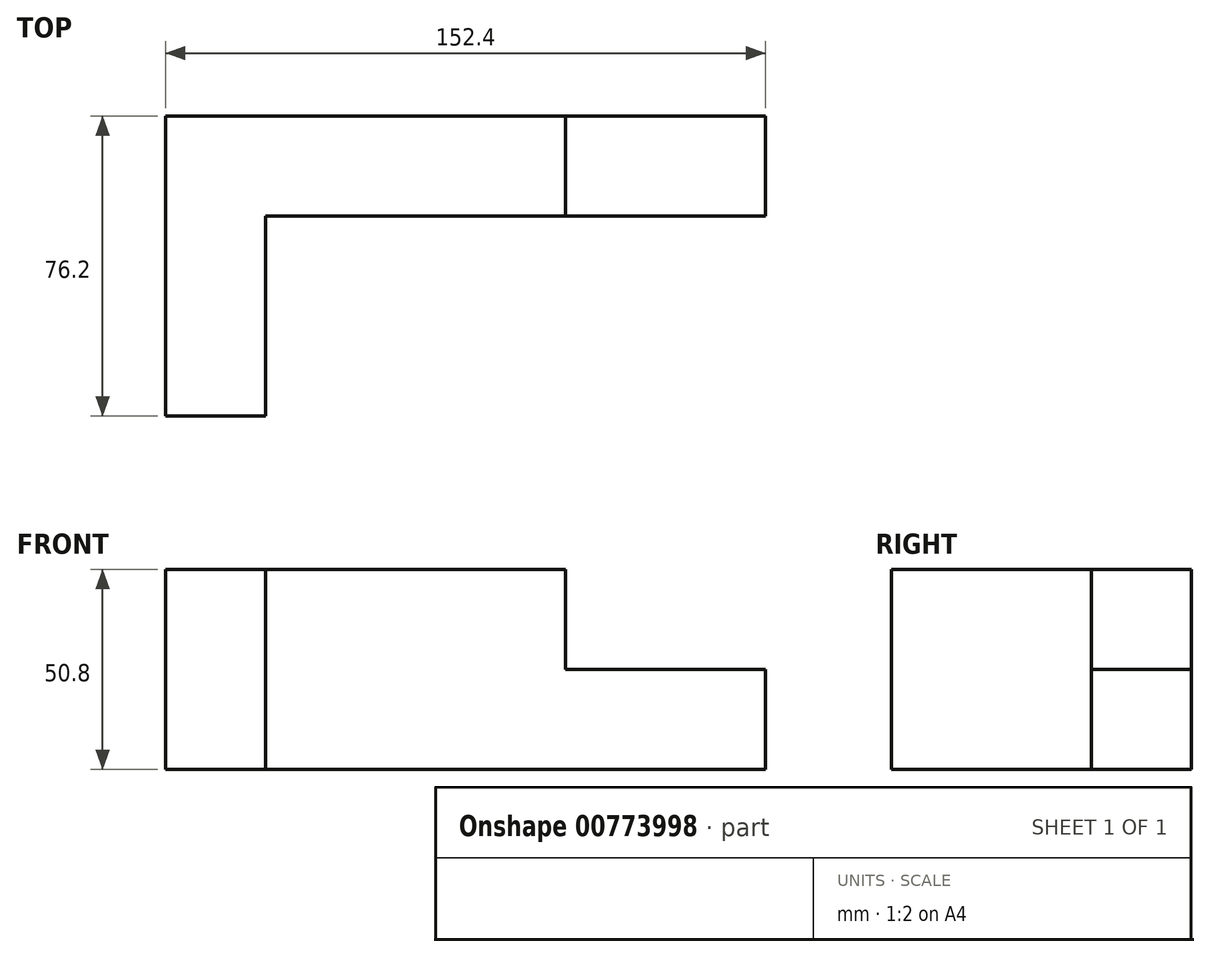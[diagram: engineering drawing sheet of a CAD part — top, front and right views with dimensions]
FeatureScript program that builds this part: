
annotation { "Feature Type Name" : "Feature", "Feature Type Description" : "" }
export const myFeature = defineFeature(function(context is Context, id is Id, definition is map)
    precondition{}
    {
        {
            var Q0;
            Q0=qCreatedBy(makeId("Front.planeOp"),FACE);
            var sketch = newSketch(context, id + "F0", { "sketchPlane" : qUnion([Q0])});
            skLineSegment(sketch, "E0", {"start": v(0, 0) * mm, "end": v(152.4, 0) * mm});
            skLineSegment(sketch, "E1", {"start": v(152.4, 0) * mm, "end": v(152.4, 50.8) * mm});
            skLineSegment(sketch, "E2", {"start": v(152.4, 50.8) * mm, "end": v(0, 50.8) * mm});
            skLineSegment(sketch, "E3", {"start": v(0, 50.8) * mm, "end": v(0, 0) * mm});
            skSolve(sketch);
        }
        {
            var Q0;
            Q0=makeQuery(id+"F0.imprint","IMPRINT",FACE,{"disambiguationData":[TD([[makeQuery(id+"F0.imprint","IMPRINT",EDGE,{"derivedFrom":sQuery(id+"F0.wireOp",EDGE,"E0")}),1.0]])]});
            extrude(context, id + "F1", {"entities" : qUnion([Q0]), "depth" : 76.2 * mm, "offsetDistance" : 25.4 * mm});
        }
        {
            var Q0;
            Q0=makeQuery(id+"F1.opExtrude","CAP_FACE",FACE,{"disambiguationData":[OSD([sQuery(id+"F0.wireOp",EDGE,"E0"),sQuery(id+"F0.wireOp",EDGE,"E1"),sQuery(id+"F0.wireOp",EDGE,"E2"),sQuery(id+"F0.wireOp",EDGE,"E3")])],"isStart":false});
            var sketch = newSketch(context, id + "F2", { "sketchPlane" : qUnion([Q0])});
            skLineSegment(sketch, "E4", {"start": v(152.4, 0) * mm, "end": v(152.4, 50.8) * mm});
            skLineSegment(sketch, "E5", {"start": v(152.4, 50.8) * mm, "end": v(25.4, 50.8) * mm});
            skLineSegment(sketch, "E6", {"start": v(25.4, 50.8) * mm, "end": v(25.4, 0) * mm});
            skLineSegment(sketch, "E7", {"start": v(25.4, 0) * mm, "end": v(152.4, 0) * mm});
            skSolve(sketch);
        }
        {
            var Q0;
            Q0=makeQuery(id+"F2.imprint","IMPRINT",FACE,{"disambiguationData":[TD([[makeQuery(id+"F2.imprint","IMPRINT",EDGE,{"derivedFrom":sQuery(id+"F2.wireOp",EDGE,"E4")}),1.0]])]});
            extrude(context, id + "F3", {"entities" : qUnion([Q0]), "operationType" : NewBodyOperationType.REMOVE, "oppositeDirection" : true, "depth" : 50.8 * mm, "offsetDistance" : 25.4 * mm});
        }
        {
            var Q0;
            Q0=makeQuery(id+"F3.boolean.opBoolean","COPY",FACE,{"derivedFrom":makeQuery(id+"F3.opExtrude","CAP_FACE",FACE,{"disambiguationData":[OSD([sQuery(id+"F2.wireOp",EDGE,"E4"),sQuery(id+"F2.wireOp",EDGE,"E5"),sQuery(id+"F2.wireOp",EDGE,"E6"),sQuery(id+"F2.wireOp",EDGE,"E7")])],"isStart":false})});
            var sketch = newSketch(context, id + "F4", { "sketchPlane" : qUnion([Q0])});
            skLineSegment(sketch, "E8", {"start": v(152.4, 50.8) * mm, "end": v(152.4, 25.4) * mm});
            skLineSegment(sketch, "E9", {"start": v(152.4, 25.4) * mm, "end": v(101.6, 25.4) * mm});
            skLineSegment(sketch, "E10", {"start": v(101.6, 25.4) * mm, "end": v(101.6, 50.8) * mm});
            skLineSegment(sketch, "E11", {"start": v(101.6, 50.8) * mm, "end": v(152.4, 50.8) * mm});
            skSolve(sketch);
        }
        {
            var Q0;
            Q0=makeQuery(id+"F4.imprint","IMPRINT",FACE,{"disambiguationData":[TD([[makeQuery(id+"F4.imprint","IMPRINT",EDGE,{"derivedFrom":sQuery(id+"F4.wireOp",EDGE,"E8")}),1.0]])]});
            extrude(context, id + "F5", {"entities" : qUnion([Q0]), "operationType" : NewBodyOperationType.REMOVE, "oppositeDirection" : true, "depth" : 25.4 * mm, "offsetDistance" : 25.4 * mm});
        }
    });
